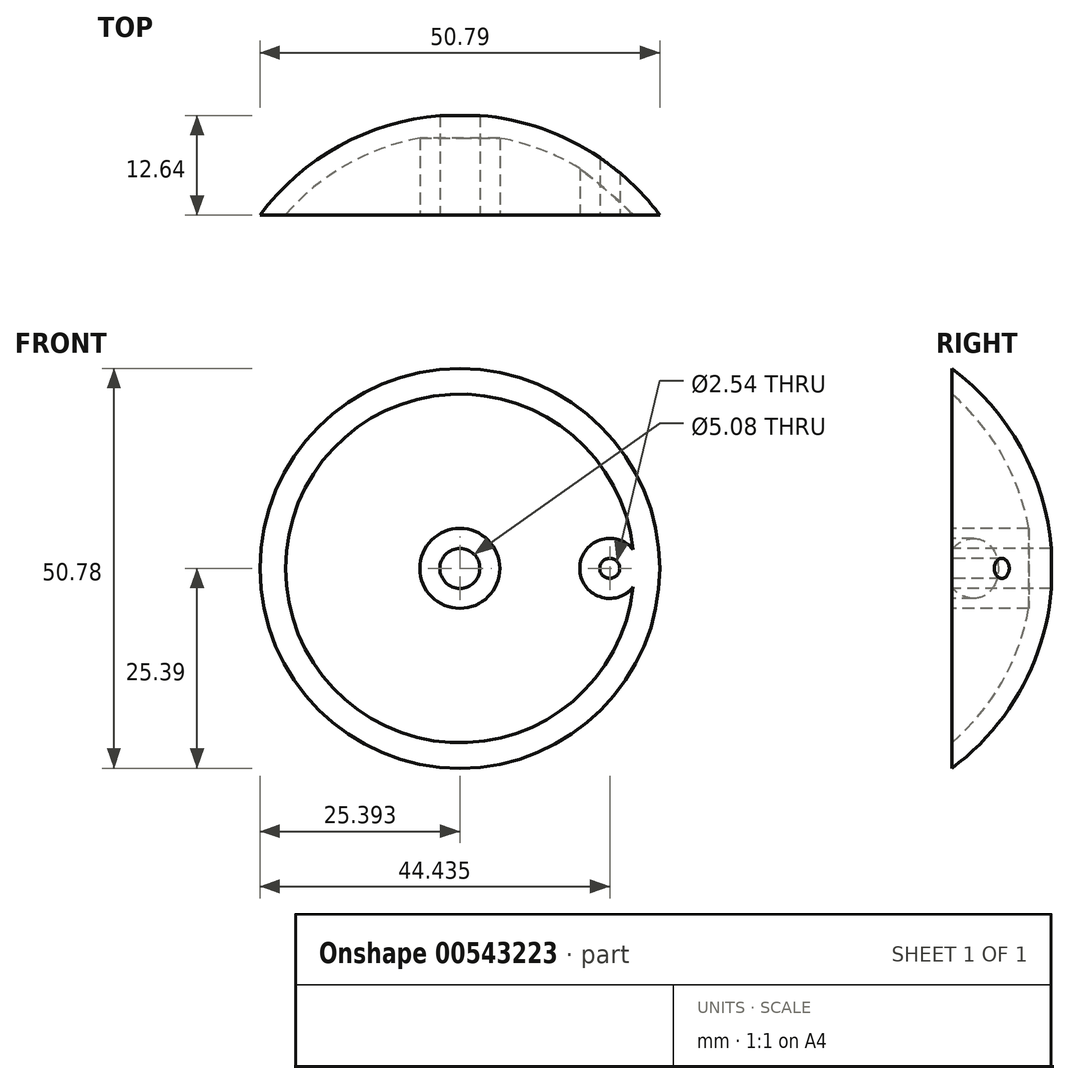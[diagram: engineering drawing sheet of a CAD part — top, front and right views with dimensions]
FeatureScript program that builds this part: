
annotation { "Feature Type Name" : "Feature", "Feature Type Description" : "" }
export const myFeature = defineFeature(function(context is Context, id is Id, definition is map)
    precondition{}
    {
        {
            var Q0;
            Q0=qCreatedBy(makeId("Top.planeOp"),FACE);
            var sketch = newSketch(context, id + "F0", { "sketchPlane" : qUnion([Q0])});
            skLineSegment(sketch, "E0", {"start": v(25.4, 0) * mm, "end": v(50.79, 0) * mm});
            skArc(sketch, "E1", {"start": v(50.79, 0) * mm, "mid": v(39.6, 9.38) * mm, "end": v(25.4, 12.74) * mm});
            skPoint(sketch, "E2", {"position": v(25.4, 0) * mm});
            skLineSegment(sketch, "E3", {"start": v(25.4, 0) * mm, "end": v(25.4, 12.74) * mm});
            skPoint(sketch, "E4.orphan", {"position": v(0, 0) * mm});
            skSolve(sketch);
        }
        {
            var Q0;
            Q0=qCreatedBy(makeId("Top.planeOp"),FACE);
            var sketch = newSketch(context, id + "F1", { "sketchPlane" : qUnion([Q0])});
            skLineSegment(sketch, "E5", {"start": v(25.4, 0) * mm, "end": v(25.4, 33.87) * mm});
            skSolve(sketch);
        }
        {
            var Q0;
            Q0=makeQuery(id+"F0.imprint","IMPRINT",FACE,{"disambiguationData":[TD([[makeQuery(id+"F0.imprint","IMPRINT",EDGE,{"derivedFrom":sQuery(id+"F0.wireOp",EDGE,"E0")}),1.0]])]});
            var Q1;
            Q1=sQuery(id+"F1.wireOp",EDGE,"E5");
            revolve(context, id + "F2", {"entities" : qUnion([Q0]), "axis" : qUnion([Q1]), "revolveType" : RevolveType.FULL});
        }
        {
            var Q0;
            Q0=makeQuery(id+"F2.opRevolve","SWEPT_FACE",FACE,{"disambiguationData":[OSD([sQuery(id+"F0.wireOp",EDGE,"E0")])]});
            var sketch = newSketch(context, id + "F3", { "sketchPlane" : qUnion([Q0])});
            skCircle(sketch, "E6.0", {"center": v(25.4, 0) * mm, "radius": 25.4 * mm, "construction": true});
            skCircle(sketch, "E7.0", {"center": v(25.4, 0) * mm, "radius": 19.04 * mm, "construction": true});
            skCircle(sketch, "E8", {"center": v(44.44, 0) * mm, "radius": 1.27 * mm});
            skSolve(sketch);
        }
        {
            var Q0;
            Q0=makeQuery(id+"F3.imprint","IMPRINT",FACE,{"disambiguationData":[TD([[makeQuery(id+"F3.imprint","IMPRINT",EDGE,{"derivedFrom":sQuery(id+"F3.wireOp",EDGE,"E8")}),1.0]])]});
            extrude(context, id + "F4", {"entities" : qUnion([Q0]), "operationType" : NewBodyOperationType.REMOVE, "endBound" : BoundingType.UP_TO_NEXT, "oppositeDirection" : true, "depth" : 25.4 * mm, "offsetDistance" : 25.4 * mm});
        }
        {
            var Q0;
            Q0=makeQuery(id+"F2.opRevolve","SWEPT_FACE",FACE,{"disambiguationData":[OSD([sQuery(id+"F0.wireOp",EDGE,"E0")])]});
            var sketch = newSketch(context, id + "F5", { "sketchPlane" : qUnion([Q0])});
            skCircle(sketch, "E9", {"center": v(25.4, 0) * mm, "radius": 2.54 * mm});
            skSolve(sketch);
        }
        {
            var Q0;
            Q0=makeQuery(id+"F5.imprint","IMPRINT",FACE,{"disambiguationData":[TD([[makeQuery(id+"F5.imprint","IMPRINT",EDGE,{"derivedFrom":sQuery(id+"F5.wireOp",EDGE,"E9")}),1.0]])]});
            extrude(context, id + "F6", {"entities" : qUnion([Q0]), "operationType" : NewBodyOperationType.REMOVE, "endBound" : BoundingType.UP_TO_NEXT, "oppositeDirection" : true, "depth" : 25.4 * mm, "offsetDistance" : 25.4 * mm});
        }
        {
            var Q0;
            Q0=makeQuery(id+"F2.opRevolve","SWEPT_FACE",FACE,{"disambiguationData":[OSD([sQuery(id+"F0.wireOp",EDGE,"E0")])]});
            shell(context, id + "F7", {"entities" : qUnion([Q0]), "thickness" : 2.54 * mm});
        }
    });
